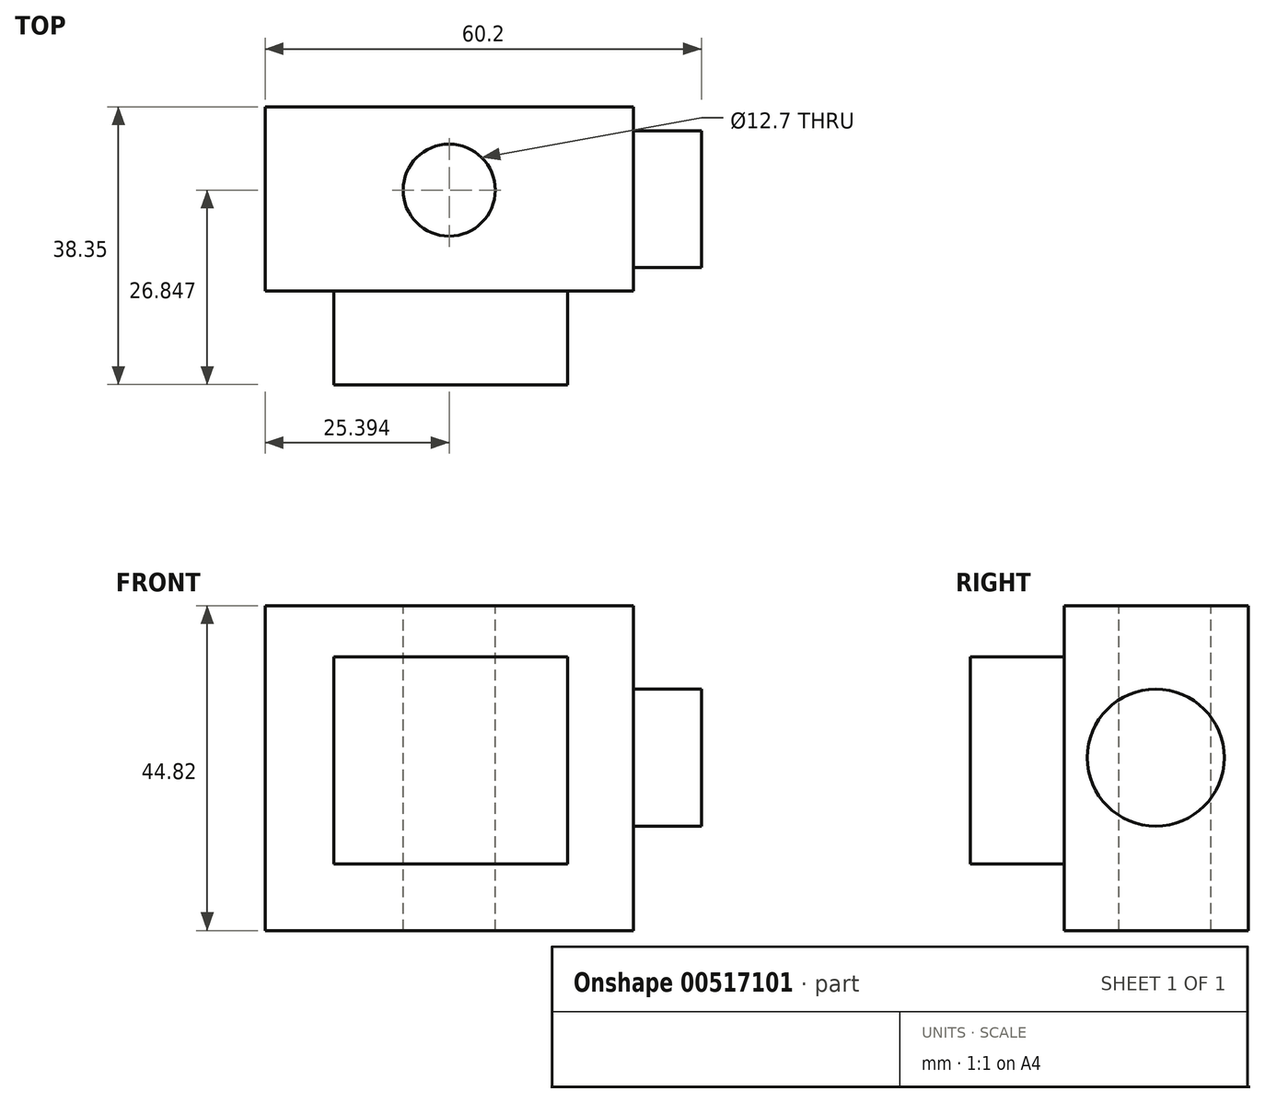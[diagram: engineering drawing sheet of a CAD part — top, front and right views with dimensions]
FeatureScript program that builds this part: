
annotation { "Feature Type Name" : "Feature", "Feature Type Description" : "" }
export const myFeature = defineFeature(function(context is Context, id is Id, definition is map)
    precondition{}
    {
        {
            var Q0;
            Q0=qCreatedBy(makeId("Front.planeOp"),FACE);
            var sketch = newSketch(context, id + "F0", { "sketchPlane" : qUnion([Q0])});
            skLineSegment(sketch, "E0.bottom", {"start": v(0, 0) * mm, "end": v(-50.8, 0) * mm});
            skLineSegment(sketch, "E0.top", {"start": v(0, 44.82) * mm, "end": v(-50.8, 44.82) * mm});
            skLineSegment(sketch, "E0.left", {"start": v(0, 0) * mm, "end": v(0, 44.82) * mm});
            skLineSegment(sketch, "E0.right", {"start": v(-50.8, 0) * mm, "end": v(-50.8, 44.82) * mm});
            skSolve(sketch);
        }
        {
            var Q0;
            Q0=makeQuery(id+"F0.imprint","IMPRINT",FACE,{"disambiguationData":[TD([[makeQuery(id+"F0.imprint","IMPRINT",EDGE,{"derivedFrom":sQuery(id+"F0.wireOp",EDGE,"E0.bottom")}),-1.0]])]});
            extrude(context, id + "F1", {"entities" : qUnion([Q0]), "depth" : 25.4 * mm, "offsetDistance" : 25.4 * mm});
        }
        {
            var Q0;
            Q0=makeQuery(id+"F1.opExtrude","SWEPT_FACE",FACE,{"disambiguationData":[OSD([sQuery(id+"F0.wireOp",EDGE,"E0.top")])]});
            var sketch = newSketch(context, id + "F2", { "sketchPlane" : qUnion([Q0])});
            skPoint(sketch, "E1", {"position": v(-25.4, -11.5) * mm});
            skSolve(sketch);
        }
        {
            var Q0;
            Q0=sQuery(id+"F2.wireOp",VERTEX,"E1");
            var Q1;
            Q1=makeQuery(id+"F1.opExtrude","SWEPT_BODY",BODY,{"disambiguationData":[OSD([sQuery(id+"F0.wireOp",EDGE,"E0.bottom"),sQuery(id+"F0.wireOp",EDGE,"E0.top"),sQuery(id+"F0.wireOp",EDGE,"E0.left"),sQuery(id+"F0.wireOp",EDGE,"E0.right")])]});
            hole(context, id + "F3", {"style" : HoleStyle.SIMPLE, "endStyle" : HoleEndStyle.THROUGH, "holeDiameter" : 12.7 * mm, "isTappedThrough" : true, "tappedDepth" : 12.7 * mm, "tapClearance" : 3, "locations" : qUnion([Q0]), "scope" : qUnion([Q1])});
        }
        {
            var Q0;
            Q0=makeQuery(id+"F1.opExtrude","CAP_FACE",FACE,{"disambiguationData":[OSD([sQuery(id+"F0.wireOp",EDGE,"E0.bottom"),sQuery(id+"F0.wireOp",EDGE,"E0.top"),sQuery(id+"F0.wireOp",EDGE,"E0.left"),sQuery(id+"F0.wireOp",EDGE,"E0.right")])],"isStart":false});
            var sketch = newSketch(context, id + "F4", { "sketchPlane" : qUnion([Q0])});
            skLineSegment(sketch, "E2.bottom", {"start": v(-41.3, 37.73) * mm, "end": v(-9.08, 37.73) * mm});
            skLineSegment(sketch, "E2.top", {"start": v(-41.3, 9.15) * mm, "end": v(-9.08, 9.15) * mm});
            skLineSegment(sketch, "E2.left", {"start": v(-41.3, 37.73) * mm, "end": v(-41.3, 9.15) * mm});
            skLineSegment(sketch, "E2.right", {"start": v(-9.08, 37.73) * mm, "end": v(-9.08, 9.15) * mm});
            skSolve(sketch);
        }
        {
            var Q0;
            Q0 = qSketchRegion(id + "F4", true);
            extrude(context, id + "F5", {"entities" : qUnion([Q0]), "operationType" : NewBodyOperationType.ADD, "depth" : 12.95 * mm, "offsetDistance" : 25.4 * mm});
        }
        {
            var Q0;
            Q0=makeQuery(id+"F1.opExtrude","SWEPT_FACE",FACE,{"disambiguationData":[OSD([sQuery(id+"F0.wireOp",EDGE,"E0.left")])]});
            var sketch = newSketch(context, id + "F6", { "sketchPlane" : qUnion([Q0])});
            skCircle(sketch, "E3", {"center": v(-12.77, 23.86) * mm, "radius": 9.45 * mm});
            skSolve(sketch);
        }
        {
            var Q0;
            Q0 = qSketchRegion(id + "F6", true);
            extrude(context, id + "F7", {"entities" : qUnion([Q0]), "operationType" : NewBodyOperationType.ADD, "depth" : 9.4 * mm, "offsetDistance" : 25.4 * mm});
        }
    });
